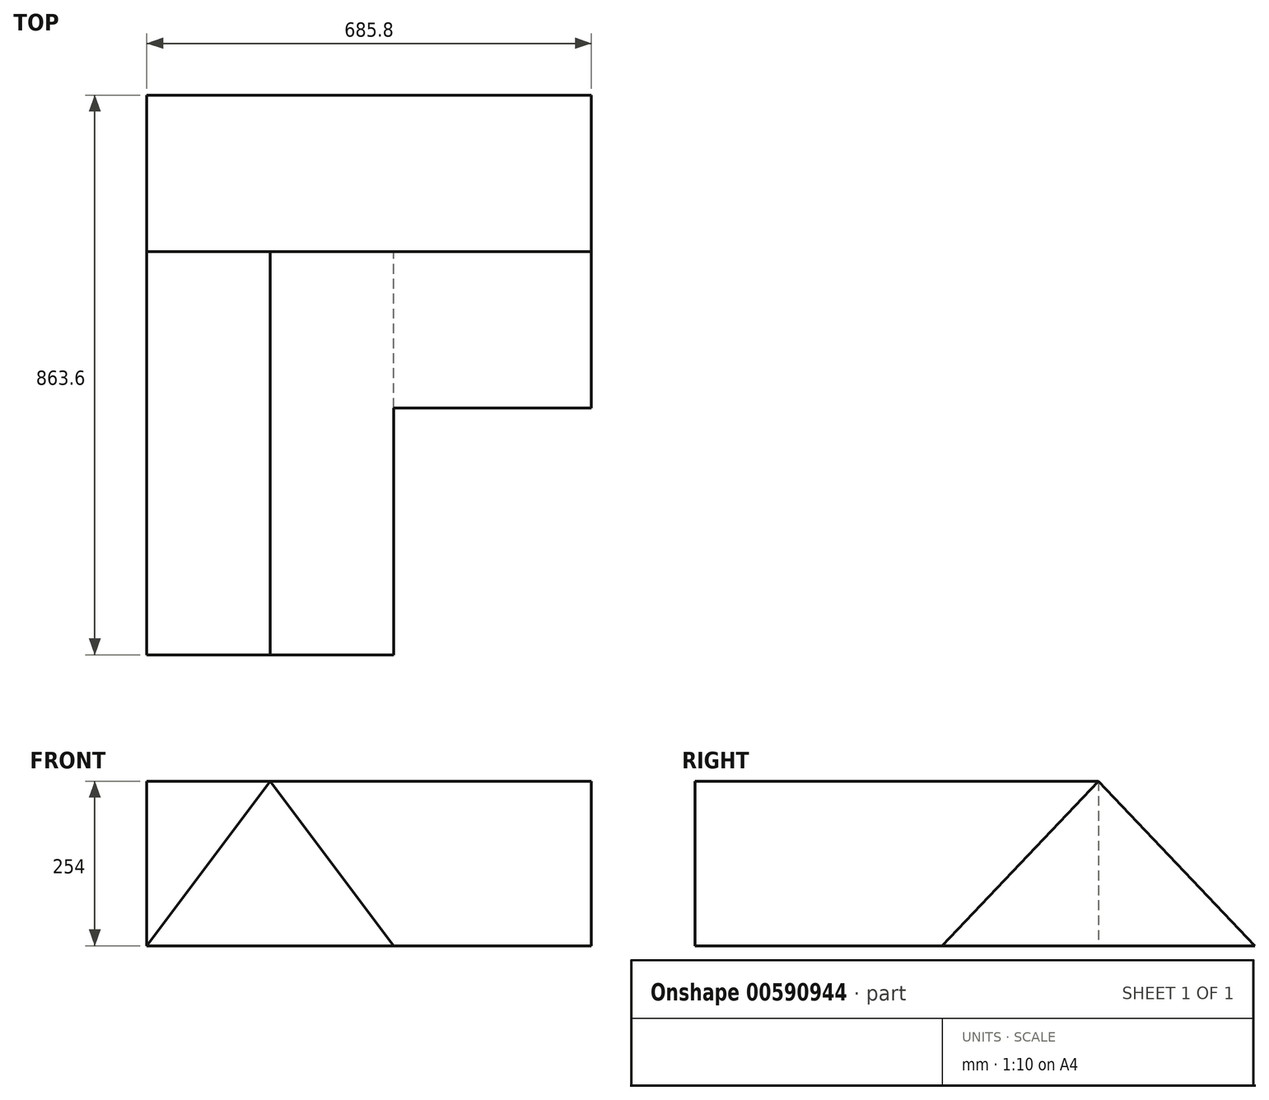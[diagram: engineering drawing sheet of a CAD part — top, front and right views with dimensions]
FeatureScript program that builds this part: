
annotation { "Feature Type Name" : "Feature", "Feature Type Description" : "" }
export const myFeature = defineFeature(function(context is Context, id is Id, definition is map)
    precondition{}
    {
        {
            var Q0;
            Q0=qCreatedBy(makeId("Top.planeOp"),FACE);
            var sketch = newSketch(context, id + "F0", { "sketchPlane" : qUnion([Q0])});
            skLineSegment(sketch, "E0", {"start": v(0, -381) * mm, "end": v(-381, -381) * mm});
            skLineSegment(sketch, "E1", {"start": v(-381, -381) * mm, "end": v(0, -381) * mm});
            skLineSegment(sketch, "E2", {"start": v(0, -381) * mm, "end": v(0, 0) * mm});
            skLineSegment(sketch, "E3", {"start": v(-381, 482.6) * mm, "end": v(-381, -381) * mm});
            skLineSegment(sketch, "E4", {"start": v(-355.6, 457.2) * mm, "end": v(-355.6, -355.6) * mm});
            skLineSegment(sketch, "E5", {"start": v(-355.6, -355.6) * mm, "end": v(-25.4, -355.6) * mm});
            skLineSegment(sketch, "E6", {"start": v(-25.4, -355.6) * mm, "end": v(-25.4, 25.4) * mm});
            skLineSegment(sketch, "E7", {"start": v(-355.6, -355.6) * mm, "end": v(-381, -355.6) * mm});
            skLineSegment(sketch, "E8", {"start": v(-355.6, -355.6) * mm, "end": v(-355.6, -381) * mm});
            skPoint(sketch, "E9.centerSnap0", {"position": v(-355.6, -368.3) * mm});
            skPoint(sketch, "E9.centerSnap1", {"position": v(-368.3, -355.6) * mm});
            skLineSegment(sketch, "E10", {"start": v(-190.5, -381) * mm, "end": v(-203.2, -381) * mm});
            skLineSegment(sketch, "E11", {"start": v(-203.2, -355.6) * mm, "end": v(-177.8, -355.6) * mm});
            skLineSegment(sketch, "E12", {"start": v(-177.8, -381) * mm, "end": v(-190.5, -381) * mm});
            skPoint(sketch, "E13.centerSnap0", {"position": v(-190.5, -355.6) * mm});
            skLineSegment(sketch, "E14", {"start": v(-381, 50.8) * mm, "end": v(-381, 38.1) * mm});
            skLineSegment(sketch, "E15", {"start": v(-355.6, 38.1) * mm, "end": v(-355.6, 63.5) * mm});
            skLineSegment(sketch, "E16", {"start": v(-381, 63.5) * mm, "end": v(-381, 50.8) * mm});
            skLineSegment(sketch, "E17", {"start": v(0, -190.5) * mm, "end": v(0, -203.2) * mm});
            skLineSegment(sketch, "E18", {"start": v(-25.4, -203.2) * mm, "end": v(-25.4, -177.8) * mm});
            skLineSegment(sketch, "E19", {"start": v(0, -177.8) * mm, "end": v(0, -190.5) * mm});
            skPoint(sketch, "E20.centerSnap1", {"position": v(-25.4, -190.5) * mm});
            skCircle(sketch, "E21", {"center": v(-368.3, -368.3) * mm, "radius": 9.53 * mm});
            skCircle(sketch, "E22.MirrorC", {"center": v(-12.7, -368.3) * mm, "radius": 9.53 * mm});
            skLineSegment(sketch, "E23.MirrorCS", {"start": v(-25.4, -355.6) * mm, "end": v(-25.4, -381) * mm});
            skLineSegment(sketch, "E24.MirrorCS", {"start": v(-25.4, -355.6) * mm, "end": v(0, -355.6) * mm});
            skLineSegment(sketch, "E25", {"start": v(-355.6, 457.2) * mm, "end": v(-381, 457.2) * mm});
            skLineSegment(sketch, "E26", {"start": v(-355.6, 457.2) * mm, "end": v(-355.6, 482.6) * mm});
            skLineSegment(sketch, "E27", {"start": v(0, 0) * mm, "end": v(-25.4, 0) * mm});
            skLineSegment(sketch, "E28", {"start": v(0, 0) * mm, "end": v(0, 25.4) * mm});
            skCircle(sketch, "E29", {"center": v(-12.7, 12.7) * mm, "radius": 9.53 * mm});
            skPoint(sketch, "E29.centerSnap0", {"position": v(0, 12.7) * mm});
            skPoint(sketch, "E29.centerSnap1", {"position": v(-12.7, 0) * mm});
            skCircle(sketch, "E30", {"center": v(-368.3, 469.9) * mm, "radius": 9.53 * mm});
            skPoint(sketch, "E30.centerSnap0", {"position": v(-368.3, 457.2) * mm});
            skPoint(sketch, "E30.centerSnap1", {"position": v(-355.6, 469.9) * mm});
            skLineSegment(sketch, "E31", {"start": v(0, 0) * mm, "end": v(279.4, 0) * mm});
            skLineSegment(sketch, "E32", {"start": v(279.4, 0) * mm, "end": v(279.4, 457.2) * mm});
            skLineSegment(sketch, "E33", {"start": v(0, 25.4) * mm, "end": v(254, 25.4) * mm});
            skLineSegment(sketch, "E34", {"start": v(254, 25.4) * mm, "end": v(254, 457.2) * mm});
            skLineSegment(sketch, "E35", {"start": v(254, 457.2) * mm, "end": v(-355.6, 457.2) * mm});
            skLineSegment(sketch, "E36", {"start": v(-381, 482.6) * mm, "end": v(279.4, 482.6) * mm});
            skLineSegment(sketch, "E37", {"start": v(254, 457.2) * mm, "end": v(254, 482.6) * mm});
            skLineSegment(sketch, "E38", {"start": v(279.4, 457.2) * mm, "end": v(279.4, 482.6) * mm});
            skLineSegment(sketch, "E39", {"start": v(254, 25.4) * mm, "end": v(254, 0) * mm});
            skLineSegment(sketch, "E40", {"start": v(254, 0) * mm, "end": v(254, 25.4) * mm});
            skLineSegment(sketch, "E41", {"start": v(279.4, 25.4) * mm, "end": v(254, 25.4) * mm});
            skLineSegment(sketch, "E42", {"start": v(-25.4, 25.4) * mm, "end": v(0, 25.4) * mm});
            skLineSegment(sketch, "E43", {"start": v(254, 457.2) * mm, "end": v(279.4, 457.2) * mm});
            skCircle(sketch, "E44", {"center": v(266.7, 469.9) * mm, "radius": 9.53 * mm});
            skPoint(sketch, "E44.centerSnap0", {"position": v(266.7, 457.2) * mm});
            skPoint(sketch, "E44.centerSnap1", {"position": v(279.4, 469.9) * mm});
            skCircle(sketch, "E45", {"center": v(266.7, 12.7) * mm, "radius": 9.53 * mm});
            skPoint(sketch, "E45.centerSnap0", {"position": v(266.7, 25.4) * mm});
            skPoint(sketch, "E45.centerSnap1", {"position": v(254, 12.7) * mm});
            skSolve(sketch);
        }
        {
            var Q0;
            Q0=qCreatedBy(makeId("Front.planeOp"),FACE);
            var sketch = newSketch(context, id + "F1", { "sketchPlane" : qUnion([Q0])});
            skPoint(sketch, "E46.0", {"position": v(0, 0) * mm});
            skPoint(sketch, "E47.0", {"position": v(-381, 0) * mm});
            skLineSegment(sketch, "E48", {"start": v(-381, 0) * mm, "end": v(0, 0) * mm});
            skLineSegment(sketch, "E49", {"start": v(-381, 0) * mm, "end": v(-190.5, 0) * mm});
            skLineSegment(sketch, "E50", {"start": v(-190.5, 0) * mm, "end": v(-190.5, 254) * mm});
            skLineSegment(sketch, "E51", {"start": v(-190.5, 254) * mm, "end": v(-381, 0) * mm});
            skLineSegment(sketch, "E52", {"start": v(-190.5, 254) * mm, "end": v(0, 0) * mm});
            skSolve(sketch);
        }
        {
            var Q0;
            Q0 = qSketchRegion(id + "F1", true);
            extrude(context, id + "F2", {"entities" : qUnion([Q0]), "depth" : 381 * mm, "offsetDistance" : 25.4 * mm, "hasSecondDirection" : true, "secondDirectionOppositeDirection" : true, "secondDirectionDepth" : 241.3 * mm});
        }
        {
            var Q0;
            Q0=qCreatedBy(makeId("Right.planeOp"),FACE);
            var sketch = newSketch(context, id + "F3", { "sketchPlane" : qUnion([Q0])});
            skPoint(sketch, "E53.0", {"position": v(0, 0) * mm});
            skPoint(sketch, "E54.0", {"position": v(482.6, 0) * mm});
            skLineSegment(sketch, "E55", {"start": v(0, 0) * mm, "end": v(482.6, 0) * mm});
            skLineSegment(sketch, "E56", {"start": v(241.3, 0) * mm, "end": v(241.3, 254) * mm});
            skLineSegment(sketch, "E57", {"start": v(241.3, 254) * mm, "end": v(0, 0) * mm});
            skLineSegment(sketch, "E58", {"start": v(241.3, 254) * mm, "end": v(482.6, 0) * mm});
            skSolve(sketch);
        }
        {
            var Q0;
            Q0 = qSketchRegion(id + "F3", true);
            extrude(context, id + "F4", {"entities" : qUnion([Q0]), "depth" : 304.8 * mm, "offsetDistance" : 25.4 * mm, "hasSecondDirection" : true, "secondDirectionOppositeDirection" : true, "secondDirectionDepth" : 381 * mm});
        }
    });
